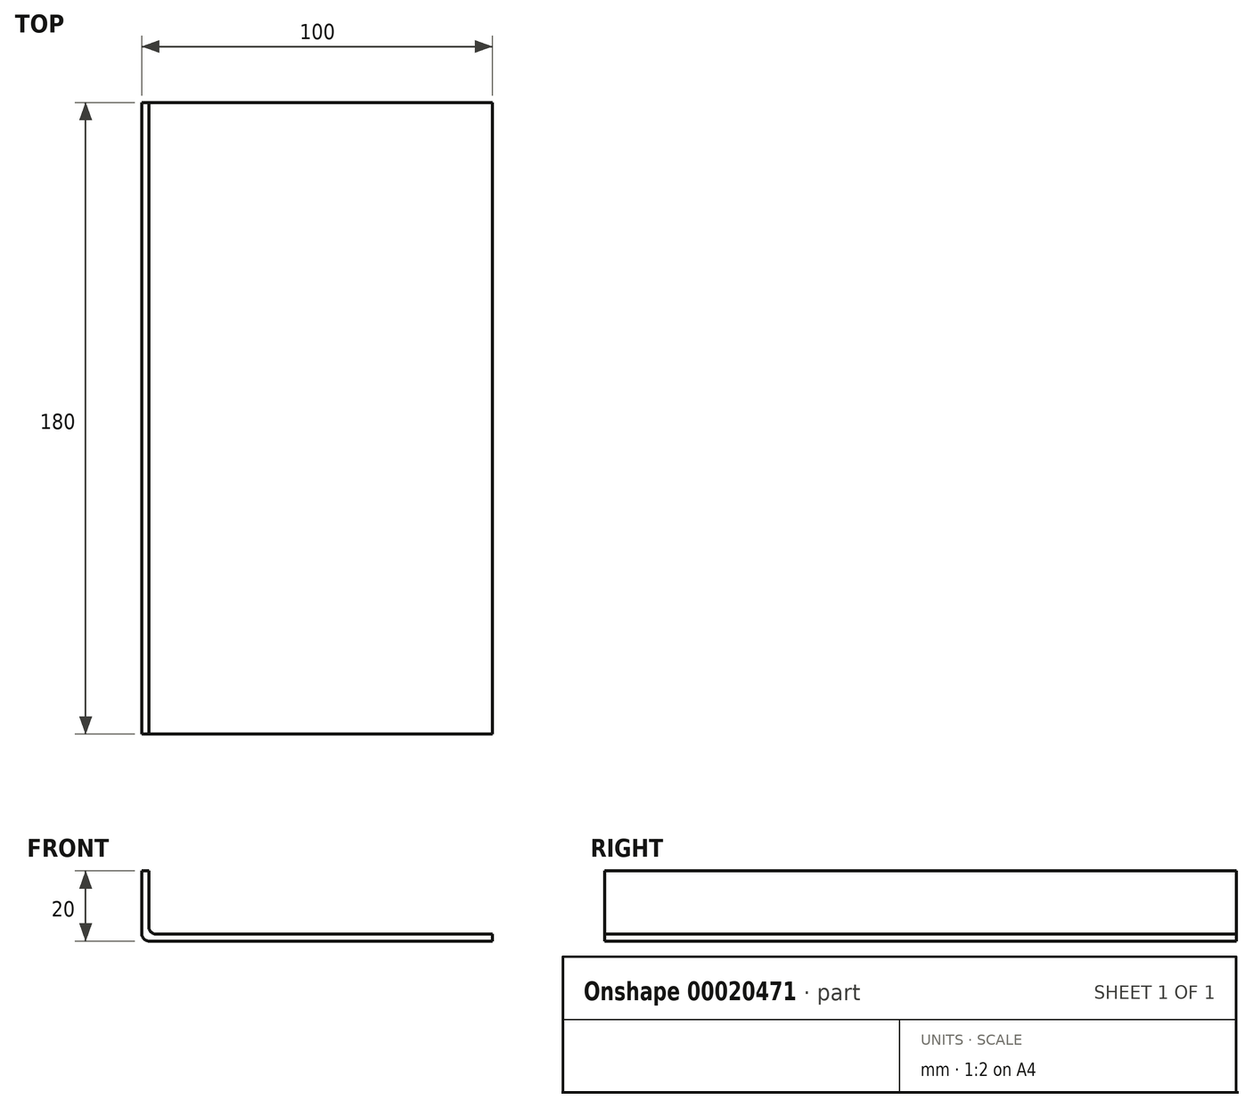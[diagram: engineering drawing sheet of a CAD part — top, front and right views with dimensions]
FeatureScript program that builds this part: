
annotation { "Feature Type Name" : "Feature", "Feature Type Description" : "" }
export const myFeature = defineFeature(function(context is Context, id is Id, definition is map)
    precondition{}
    {
        {
            var Q0;
            Q0=qCreatedBy(makeId("Front.planeOp"),FACE);
            var sketch = newSketch(context, id + "F0", { "sketchPlane" : qUnion([Q0])});
            skLineSegment(sketch, "E0", {"start": v(0, 0) * mm, "end": v(100, 0) * mm});
            skLineSegment(sketch, "E1", {"start": v(0, 0) * mm, "end": v(0, 20) * mm});
            skLineSegment(sketch, "E2", {"start": v(0, 20) * mm, "end": v(2, 20) * mm});
            skLineSegment(sketch, "E3", {"start": v(2, 20) * mm, "end": v(2, 2) * mm});
            skLineSegment(sketch, "E4", {"start": v(2, 2) * mm, "end": v(100, 2) * mm});
            skLineSegment(sketch, "E5", {"start": v(100, 2) * mm, "end": v(100, 0) * mm});
            skSolve(sketch);
        }
        {
            var Q0;
            Q0=makeQuery(id+"F0.imprint","IMPRINT",FACE,{"disambiguationData":[TD([[makeQuery(id+"F0.imprint","IMPRINT",EDGE,{"derivedFrom":sQuery(id+"F0.wireOp",EDGE,"E0")}),1.0]])]});
            extrude(context, id + "F1", {"entities" : qUnion([Q0]), "depth" : 180 * mm});
        }
        {
            var Q0;
            Q0=makeQuery(id+"F1.opExtrude","SWEPT_EDGE",EDGE,{"disambiguationData":[OSD([sQuery(id+"F0.wireOp",EDGE,"E3"),sQuery(id+"F0.wireOp",EDGE,"E4")])]});
            var Q1;
            Q1=makeQuery(id+"F1.opExtrude","SWEPT_EDGE",EDGE,{"disambiguationData":[OSD([sQuery(id+"F0.wireOp",EDGE,"E0"),sQuery(id+"F0.wireOp",EDGE,"E1")])]});
            fillet(context, id + "F2", {"entities" : qUnion([Q0, Q1]), "radius" : 2 * mm, "tangentPropagation" : true, "allowEdgeOverflow" : false});
        }
    });
